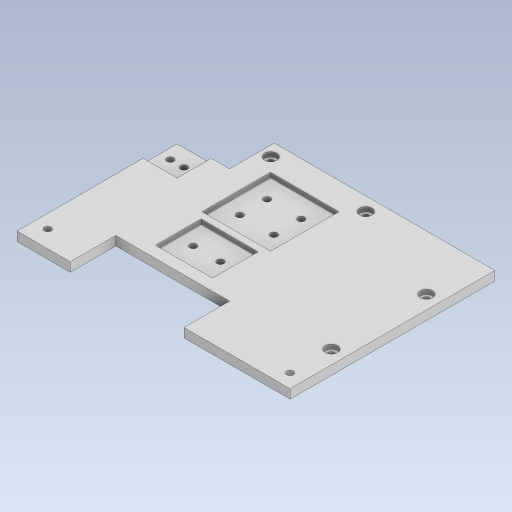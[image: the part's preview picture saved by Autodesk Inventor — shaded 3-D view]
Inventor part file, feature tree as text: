
AUTODESK INVENTOR PART (.ipt)
format: ipt  version: 2023.5 (Build 275446000, 446)  size: 385,536 bytes
history: native  units: in
note: dims shown in document units (in); Inventor stores cm internally (conversion verified against a paired STEP export)
features: extrude x2, sketch x1
ambient origin geometry x8: Origin, YZ Plane, XZ Plane, XY Plane, X Axis, Y Axis, Z Axis, Center Point
bodies: Body1 (feature_tree)
feature tree (3):
  sketch  "Sketch1"  dims[d0=4.7244in d1=3.5433in d21=0.1181in d22=0.2559in d23=0.1181in d24=0.2559in d25=0.1181in d27=0.1181in d32=0.1969in d38=0.1181in d39=0.2165in d40=0.2362in d41=0.2165in d42=0.1181in d43=0.2362in d44=0.2362in d45=0.1181in d46=0.2362in d59=0.7736in d60=0.1181in d61=0.1969in d63=0.2953in d64=0.1575in d65=0.0in d66=0.0787in d67=0.0in d68=0.1181in d69=0.1181in d70=0.8219in d71=0.8219in d72=0.2165in d73=0.2165in d74=0.0in d75=0.0in d76=0.2953in d77=0.2953in d78=0.2953in d79=0.2953in d81=0.315in d33=0.0197in d34=0.0344in d35=0.0197in d36=0.0344in]
  extrude  "Extrusion3"  Depth=3.5433in
  extrude  "Extrusion4"  Depth=0.1181in
